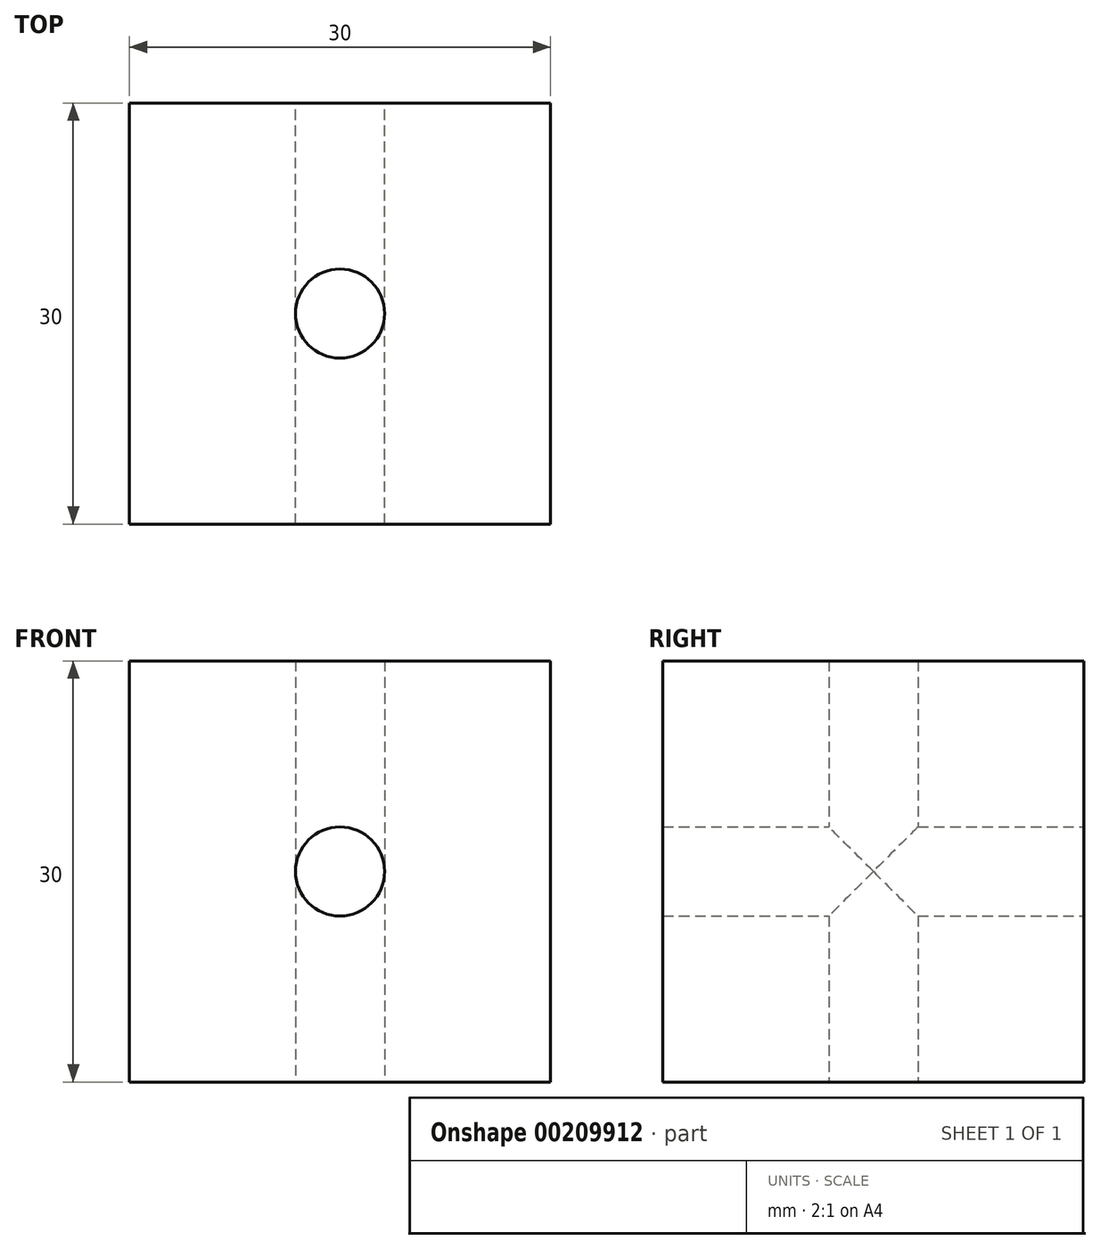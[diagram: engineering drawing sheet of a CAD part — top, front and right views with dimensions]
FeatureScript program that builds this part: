
annotation { "Feature Type Name" : "Feature", "Feature Type Description" : "" }
export const myFeature = defineFeature(function(context is Context, id is Id, definition is map)
    precondition{}
    {
        {
            var Q0;
            Q0=qCreatedBy(makeId("Front.planeOp"),FACE);
            var sketch = newSketch(context, id + "F0", { "sketchPlane" : qUnion([Q0])});
            skLineSegment(sketch, "E0.bottom", {"start": v(0, 0) * mm, "end": v(-30, 0) * mm});
            skLineSegment(sketch, "E0.top", {"start": v(0, 30) * mm, "end": v(-30, 30) * mm});
            skLineSegment(sketch, "E0.left", {"start": v(0, 0) * mm, "end": v(0, 30) * mm});
            skLineSegment(sketch, "E0.right", {"start": v(-30, 0) * mm, "end": v(-30, 30) * mm});
            skSolve(sketch);
        }
        {
            var Q0;
            Q0 = qSketchRegion(id + "F0", true);
            extrude(context, id + "F1", {"entities" : qUnion([Q0]), "depth" : 30 * mm});
        }
        {
            var Q0;
            Q0=makeQuery(id+"F1.opExtrude","CAP_FACE",FACE,{"disambiguationData":[OSD([sQuery(id+"F0.wireOp",EDGE,"E0.bottom"),sQuery(id+"F0.wireOp",EDGE,"E0.top"),sQuery(id+"F0.wireOp",EDGE,"E0.left"),sQuery(id+"F0.wireOp",EDGE,"E0.right")])],"isStart":true});
            var sketch = newSketch(context, id + "F2", { "sketchPlane" : qUnion([Q0])});
            skCircle(sketch, "E1", {"center": v(15, 15) * mm, "radius": 3.18 * mm});
            skSolve(sketch);
        }
        {
            var Q0;
            Q0 = qSketchRegion(id + "F2", true);
            extrude(context, id + "F3", {"entities" : qUnion([Q0]), "operationType" : NewBodyOperationType.REMOVE, "endBound" : BoundingType.THROUGH_ALL, "oppositeDirection" : true, "depth" : 25 * mm});
        }
        {
            var Q0;
            Q0=makeQuery(id+"F1.opExtrude","SWEPT_FACE",FACE,{"disambiguationData":[OSD([sQuery(id+"F0.wireOp",EDGE,"E0.bottom")])]});
            var sketch = newSketch(context, id + "F4", { "sketchPlane" : qUnion([Q0])});
            skCircle(sketch, "E2", {"center": v(-15, 15) * mm, "radius": 3.18 * mm});
            skSolve(sketch);
        }
        {
            var Q0;
            Q0 = qSketchRegion(id + "F4", true);
            extrude(context, id + "F5", {"entities" : qUnion([Q0]), "operationType" : NewBodyOperationType.REMOVE, "endBound" : BoundingType.THROUGH_ALL, "oppositeDirection" : true, "depth" : 25 * mm});
        }
    });
